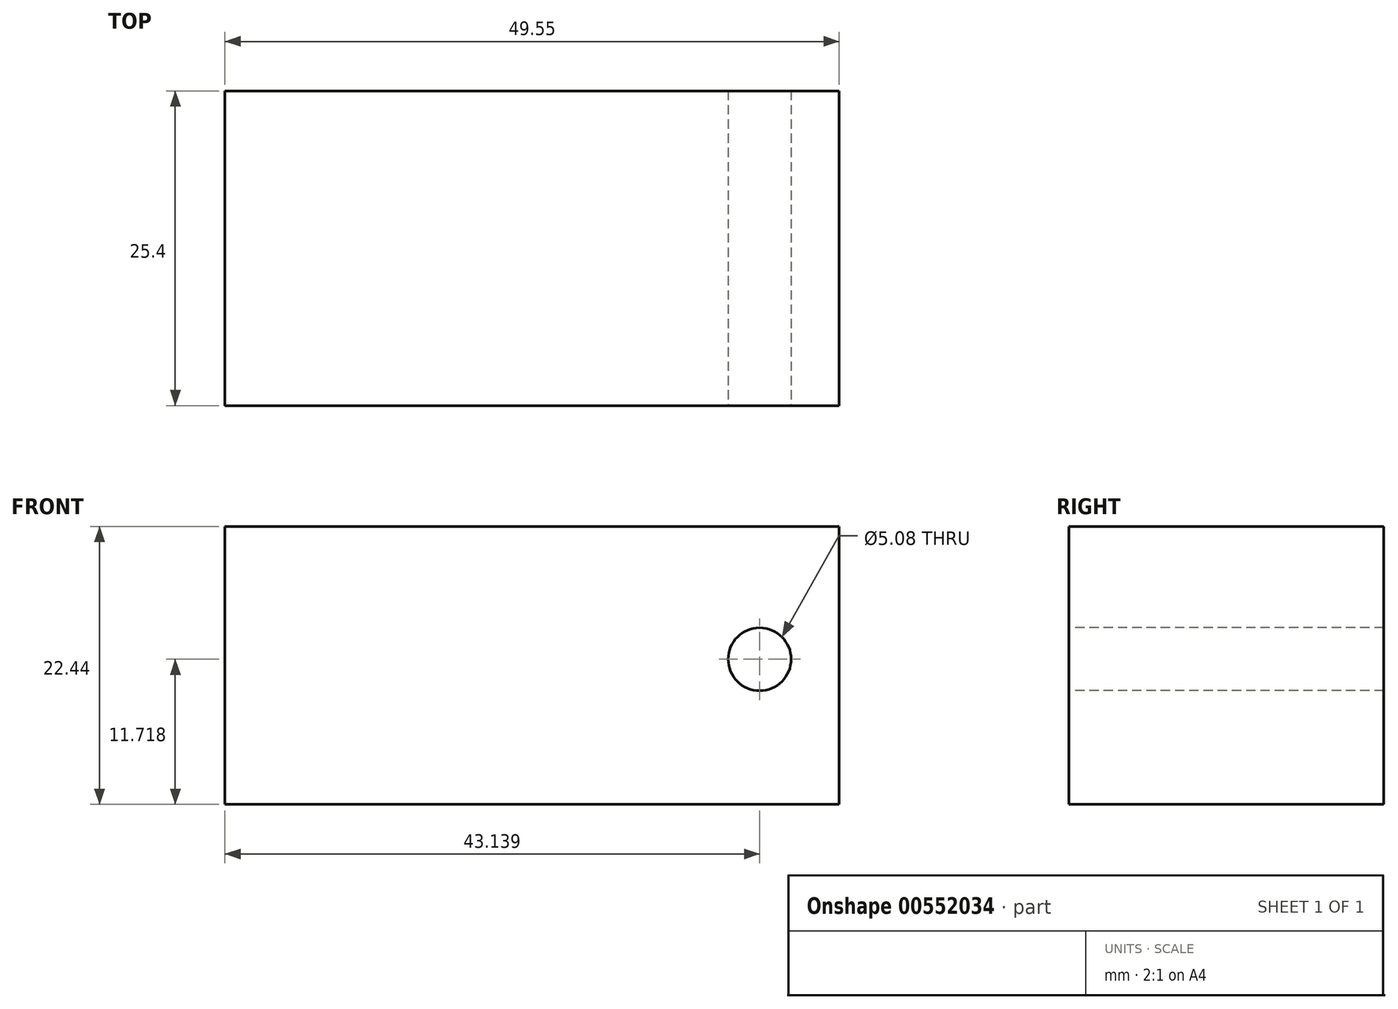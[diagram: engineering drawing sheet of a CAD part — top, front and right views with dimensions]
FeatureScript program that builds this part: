
annotation { "Feature Type Name" : "Feature", "Feature Type Description" : "" }
export const myFeature = defineFeature(function(context is Context, id is Id, definition is map)
    precondition{}
    {
        {
            var Q0;
            Q0=qCreatedBy(makeId("Front.planeOp"),FACE);
            var sketch = newSketch(context, id + "F0", { "sketchPlane" : qUnion([Q0])});
            skLineSegment(sketch, "E0.bottom", {"start": v(-59.38, 56.34) * mm, "end": v(-9.83, 56.34) * mm});
            skLineSegment(sketch, "E0.top", {"start": v(-59.38, 33.9) * mm, "end": v(-9.83, 33.9) * mm});
            skLineSegment(sketch, "E0.left", {"start": v(-59.38, 56.34) * mm, "end": v(-59.38, 33.9) * mm});
            skLineSegment(sketch, "E0.right", {"start": v(-9.83, 56.34) * mm, "end": v(-9.83, 33.9) * mm});
            skSolve(sketch);
        }
        {
            var Q0;
            Q0 = qSketchRegion(id + "F0", true);
            extrude(context, id + "F1", {"entities" : qUnion([Q0]), "depth" : 25.4 * mm, "offsetDistance" : 25.4 * mm});
        }
        {
            var Q0;
            Q0=makeQuery(id+"F1.opExtrude","CAP_FACE",FACE,{"disambiguationData":[OSD([sQuery(id+"F0.wireOp",EDGE,"E0.bottom"),sQuery(id+"F0.wireOp",EDGE,"E0.top"),sQuery(id+"F0.wireOp",EDGE,"E0.left"),sQuery(id+"F0.wireOp",EDGE,"E0.right")])],"isStart":false});
            var sketch = newSketch(context, id + "F2", { "sketchPlane" : qUnion([Q0])});
            skCircle(sketch, "E1", {"center": v(-16.24, 45.62) * mm, "radius": 5.34 * mm});
            skSolve(sketch);
        }
        {
            var Q0;
            Q0=sQuery(id+"F2.wireOp",VERTEX,"E1.center");
            var Q1;
            Q1=makeQuery(id+"F1.opExtrude","SWEPT_BODY",BODY,{"disambiguationData":[OSD([sQuery(id+"F0.wireOp",EDGE,"E0.bottom"),sQuery(id+"F0.wireOp",EDGE,"E0.top"),sQuery(id+"F0.wireOp",EDGE,"E0.left"),sQuery(id+"F0.wireOp",EDGE,"E0.right")])]});
            hole(context, id + "F3", {"style" : HoleStyle.SIMPLE, "endStyle" : HoleEndStyle.THROUGH, "holeDiameter" : 5.08 * mm, "isTappedThrough" : true, "tappedDepth" : 12.7 * mm, "tapClearance" : 3, "locations" : qUnion([Q0]), "scope" : qUnion([Q1])});
        }
    });
